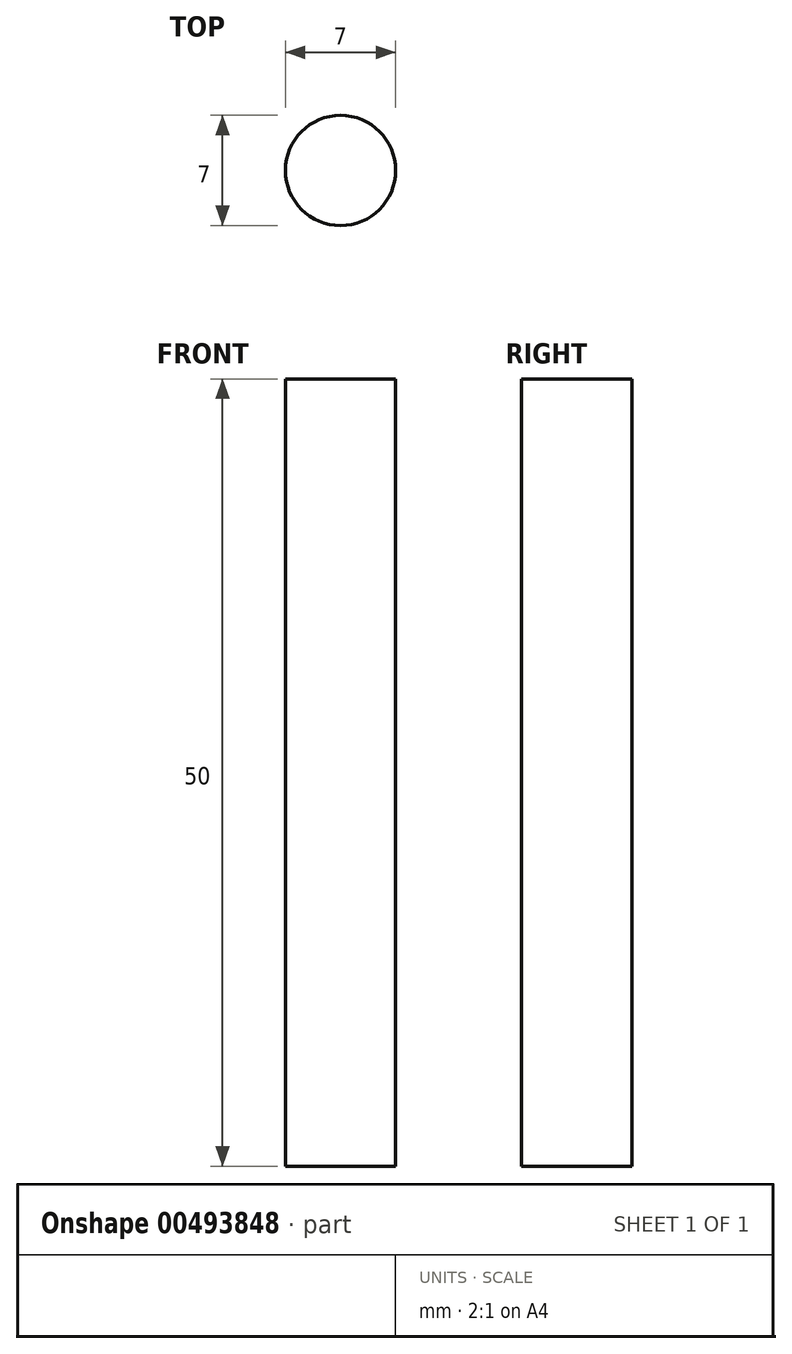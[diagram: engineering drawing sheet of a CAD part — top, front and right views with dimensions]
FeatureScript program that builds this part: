
annotation { "Feature Type Name" : "Feature", "Feature Type Description" : "" }
export const myFeature = defineFeature(function(context is Context, id is Id, definition is map)
    precondition{}
    {
        {
            var Q0;
            Q0=qCreatedBy(makeId("Top.planeOp"),FACE);
            var sketch = newSketch(context, id + "F0", { "sketchPlane" : qUnion([Q0])});
            skCircle(sketch, "E0", {"center": v(-93.49, -11.78) * mm, "radius": 3.5 * mm});
            skSolve(sketch);
        }
        {
            var Q0;
            Q0 = qSketchRegion(id + "F0", true);
            extrude(context, id + "F1", {"entities" : qUnion([Q0]), "depth" : 50 * mm});
        }
    });
